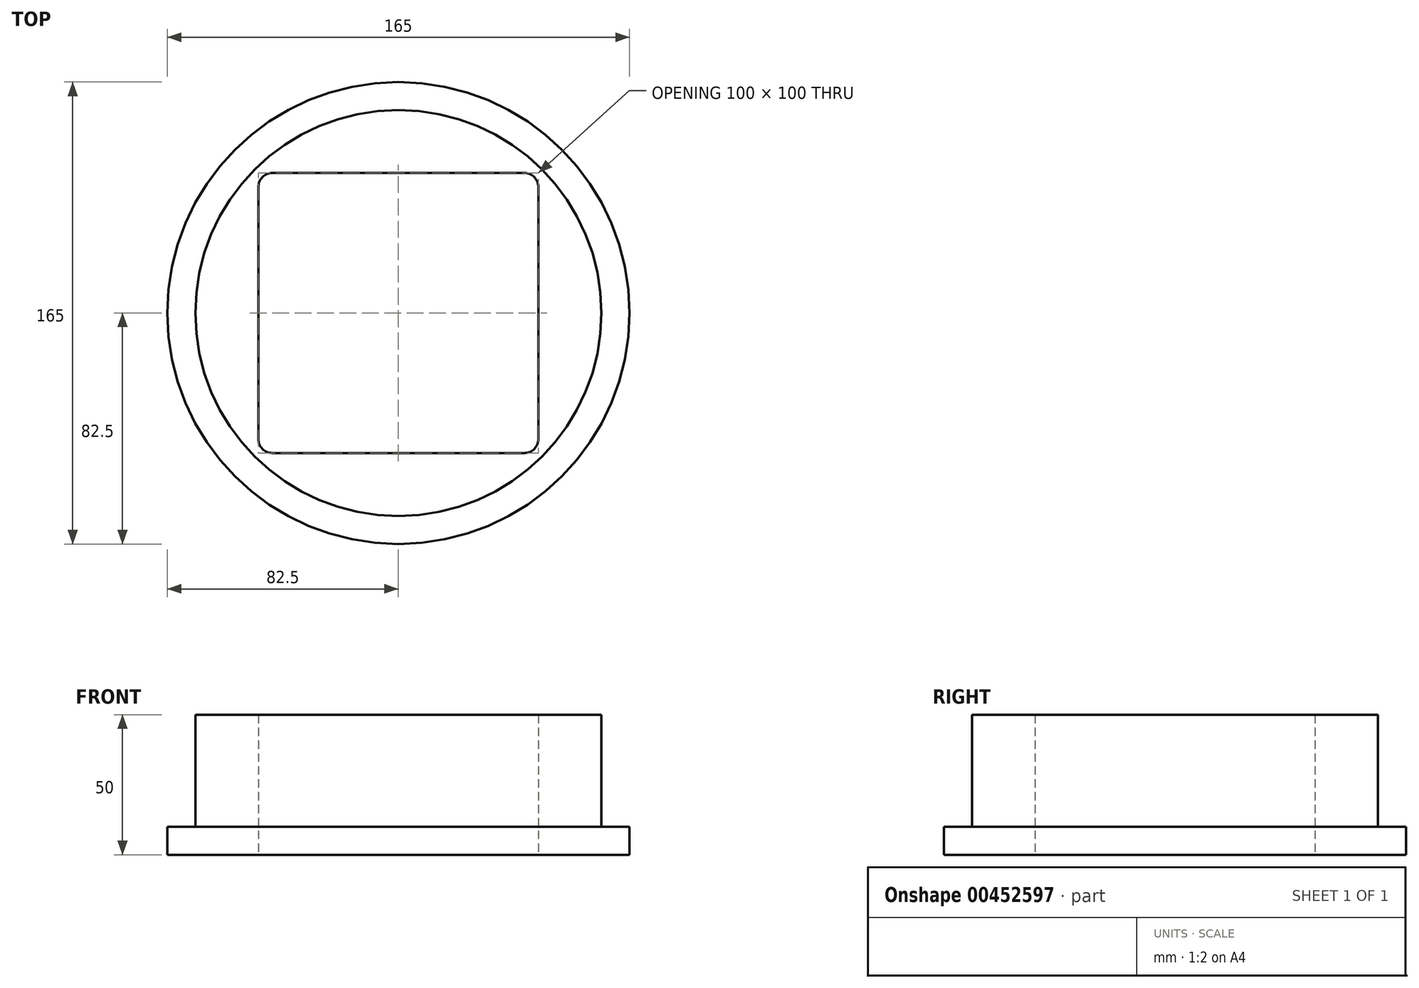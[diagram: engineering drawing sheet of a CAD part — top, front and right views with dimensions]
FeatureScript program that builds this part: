
annotation { "Feature Type Name" : "Feature", "Feature Type Description" : "" }
export const myFeature = defineFeature(function(context is Context, id is Id, definition is map)
    precondition{}
    {
        {
            var Q0;
            Q0=qCreatedBy(makeId("Top.planeOp"),FACE);
            var sketch = newSketch(context, id + "F0", { "sketchPlane" : qUnion([Q0])});
            skCircle(sketch, "E0", {"center": v(0, 0) * mm, "radius": 72.5 * mm});
            skLineSegment(sketch, "E1.bottom", {"start": v(45, -50) * mm, "end": v(-45, -50) * mm});
            skLineSegment(sketch, "E1.top", {"start": v(45, 50) * mm, "end": v(-45, 50) * mm});
            skLineSegment(sketch, "E1.left", {"start": v(50, -45) * mm, "end": v(50, 45) * mm});
            skLineSegment(sketch, "E1.right", {"start": v(-50, -45) * mm, "end": v(-50, 45) * mm});
            skCircle(sketch, "E2", {"center": v(0, 0) * mm, "radius": 82.5 * mm});
            skPoint(sketch, "E3.middle", {"position": v(-50, 0) * mm});
            skPoint(sketch, "E4.middle", {"position": v(50, 0) * mm});
            skPoint(sketch, "E5.visualSharp", {"position": v(-50, 50) * mm});
            skArc(sketch, "E5.filletArc", {"start": v(-45, 50) * mm, "mid": v(-48.54, 48.54) * mm, "end": v(-50, 45) * mm});
            skPoint(sketch, "E6.visualSharp", {"position": v(50, 50) * mm});
            skArc(sketch, "E6.filletArc", {"start": v(50, 45) * mm, "mid": v(48.54, 48.54) * mm, "end": v(45, 50) * mm});
            skPoint(sketch, "E7.visualSharp", {"position": v(50, -50) * mm});
            skArc(sketch, "E7.filletArc", {"start": v(45, -50) * mm, "mid": v(48.54, -48.54) * mm, "end": v(50, -45) * mm});
            skPoint(sketch, "E8.visualSharp", {"position": v(-50, -50) * mm});
            skArc(sketch, "E8.filletArc", {"start": v(-50, -45) * mm, "mid": v(-48.54, -48.54) * mm, "end": v(-45, -50) * mm});
            skSolve(sketch);
        }
        {
            var Q0;
            Q0=makeQuery(id+"F0.imprint","IMPRINT",FACE,{"disambiguationData":[TD([[makeQuery(id+"F0.imprint","IMPRINT",EDGE,{"derivedFrom":sQuery(id+"F0.wireOp",EDGE,"E0")}),1.0]])]});
            extrude(context, id + "F1", {"entities" : qUnion([Q0]), "depth" : 50 * mm});
        }
        {
            var Q0;
            Q0 = qSketchRegion(id + "F0", true);
            extrude(context, id + "F2", {"entities" : qUnion([Q0]), "operationType" : NewBodyOperationType.ADD, "depth" : 10 * mm});
        }
    });
